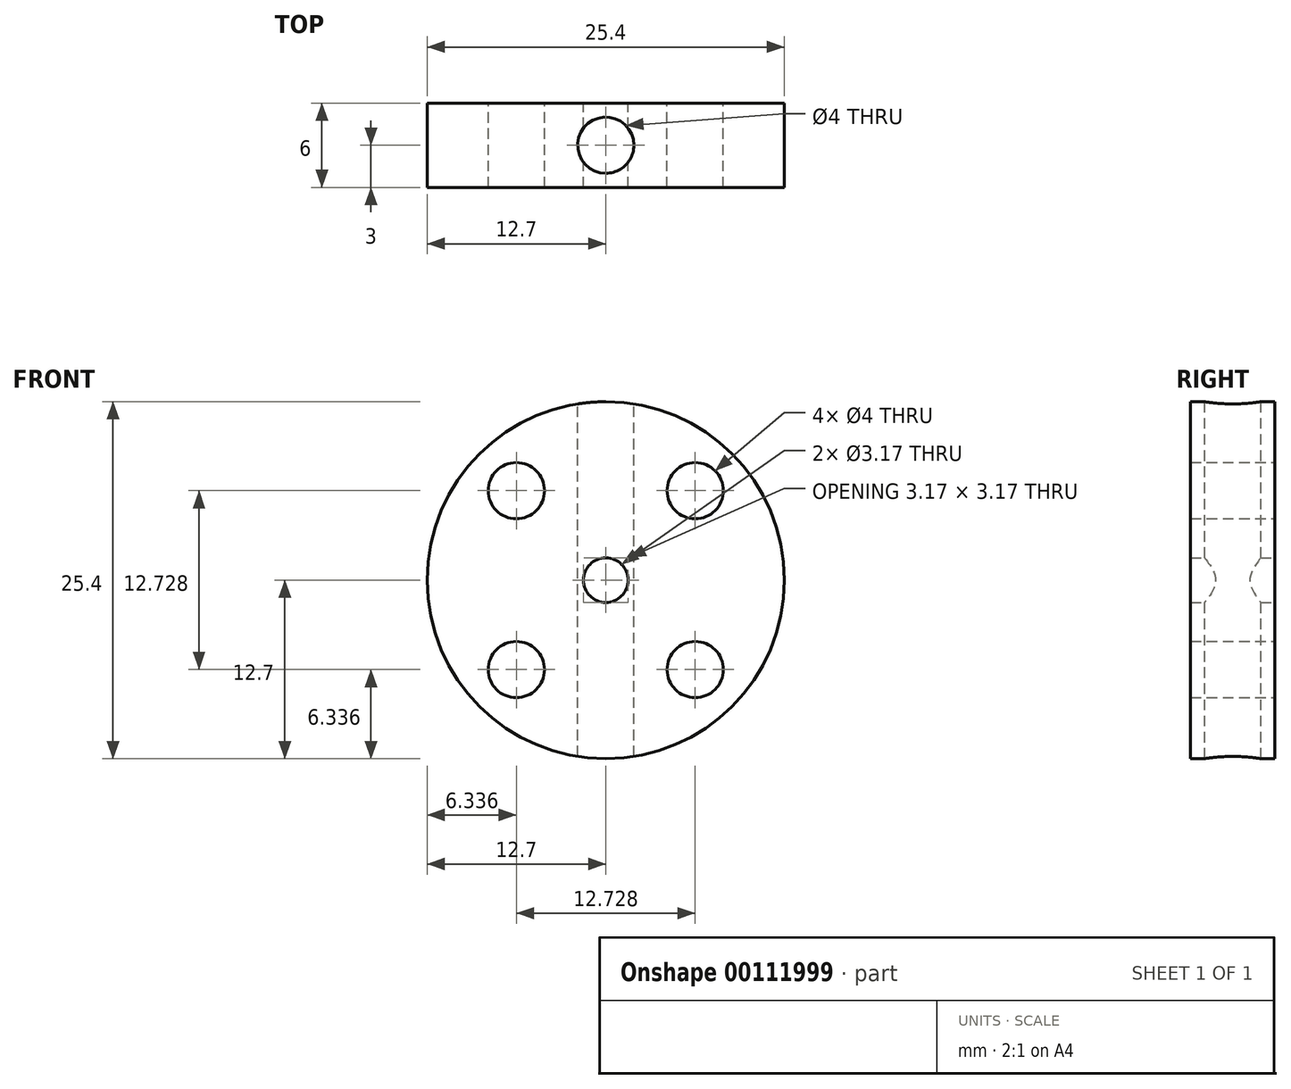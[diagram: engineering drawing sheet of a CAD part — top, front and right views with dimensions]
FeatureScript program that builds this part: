
annotation { "Feature Type Name" : "Feature", "Feature Type Description" : "" }
export const myFeature = defineFeature(function(context is Context, id is Id, definition is map)
    precondition{}
    {
        {
            var Q0;
            Q0=qCreatedBy(makeId("Front.planeOp"),FACE);
            var sketch = newSketch(context, id + "F0", { "sketchPlane" : qUnion([Q0])});
            skCircle(sketch, "E0", {"center": v(0, 0) * mm, "radius": 12.7 * mm});
            skCircle(sketch, "E1", {"center": v(0, 0) * mm, "radius": 9 * mm, "construction": true});
            skLineSegment(sketch, "E2.bottom", {"start": v(-6.36, 6.36) * mm, "end": v(6.36, 6.36) * mm, "construction": true});
            skLineSegment(sketch, "E2.top", {"start": v(-6.36, -6.36) * mm, "end": v(6.36, -6.36) * mm, "construction": true});
            skLineSegment(sketch, "E2.left", {"start": v(-6.36, 6.36) * mm, "end": v(-6.36, -6.36) * mm, "construction": true});
            skLineSegment(sketch, "E2.right", {"start": v(6.36, 6.36) * mm, "end": v(6.36, -6.36) * mm, "construction": true});
            skCircle(sketch, "E3", {"center": v(-6.36, 6.36) * mm, "radius": 2 * mm});
            skCircle(sketch, "E4", {"center": v(6.36, 6.36) * mm, "radius": 2 * mm});
            skCircle(sketch, "E5", {"center": v(6.36, -6.36) * mm, "radius": 2 * mm});
            skCircle(sketch, "E6", {"center": v(-6.36, -6.36) * mm, "radius": 2 * mm});
            skCircle(sketch, "E7", {"center": v(0, 0) * mm, "radius": 1.59 * mm});
            skSolve(sketch);
        }
        {
            var Q0;
            Q0=makeQuery(id+"F0.imprint","IMPRINT",FACE,{"disambiguationData":[TD([[makeQuery(id+"F0.imprint","IMPRINT",EDGE,{"derivedFrom":sQuery(id+"F0.wireOp",EDGE,"E0")}),1.0]])]});
            extrude(context, id + "F1", {"entities" : qUnion([Q0]), "depth" : 6 * mm});
        }
        {
            var Q0;
            Q0=qCreatedBy(makeId("Top.planeOp"),FACE);
            var sketch = newSketch(context, id + "F2", { "sketchPlane" : qUnion([Q0])});
            skCircle(sketch, "E8", {"center": v(0, -3) * mm, "radius": 2 * mm});
            skSolve(sketch);
        }
        {
            var Q0;
            Q0 = qSketchRegion(id + "F2", true);
            extrude(context, id + "F3", {"entities" : qUnion([Q0]), "operationType" : NewBodyOperationType.REMOVE, "endBound" : BoundingType.THROUGH_ALL, "oppositeDirection" : true, "depth" : 25 * mm, "hasSecondDirection" : true, "secondDirectionBound" : SecondDirectionBoundingType.THROUGH_ALL, "secondDirectionOppositeDirection" : false, "secondDirectionDepth" : 25 * mm});
        }
    });
